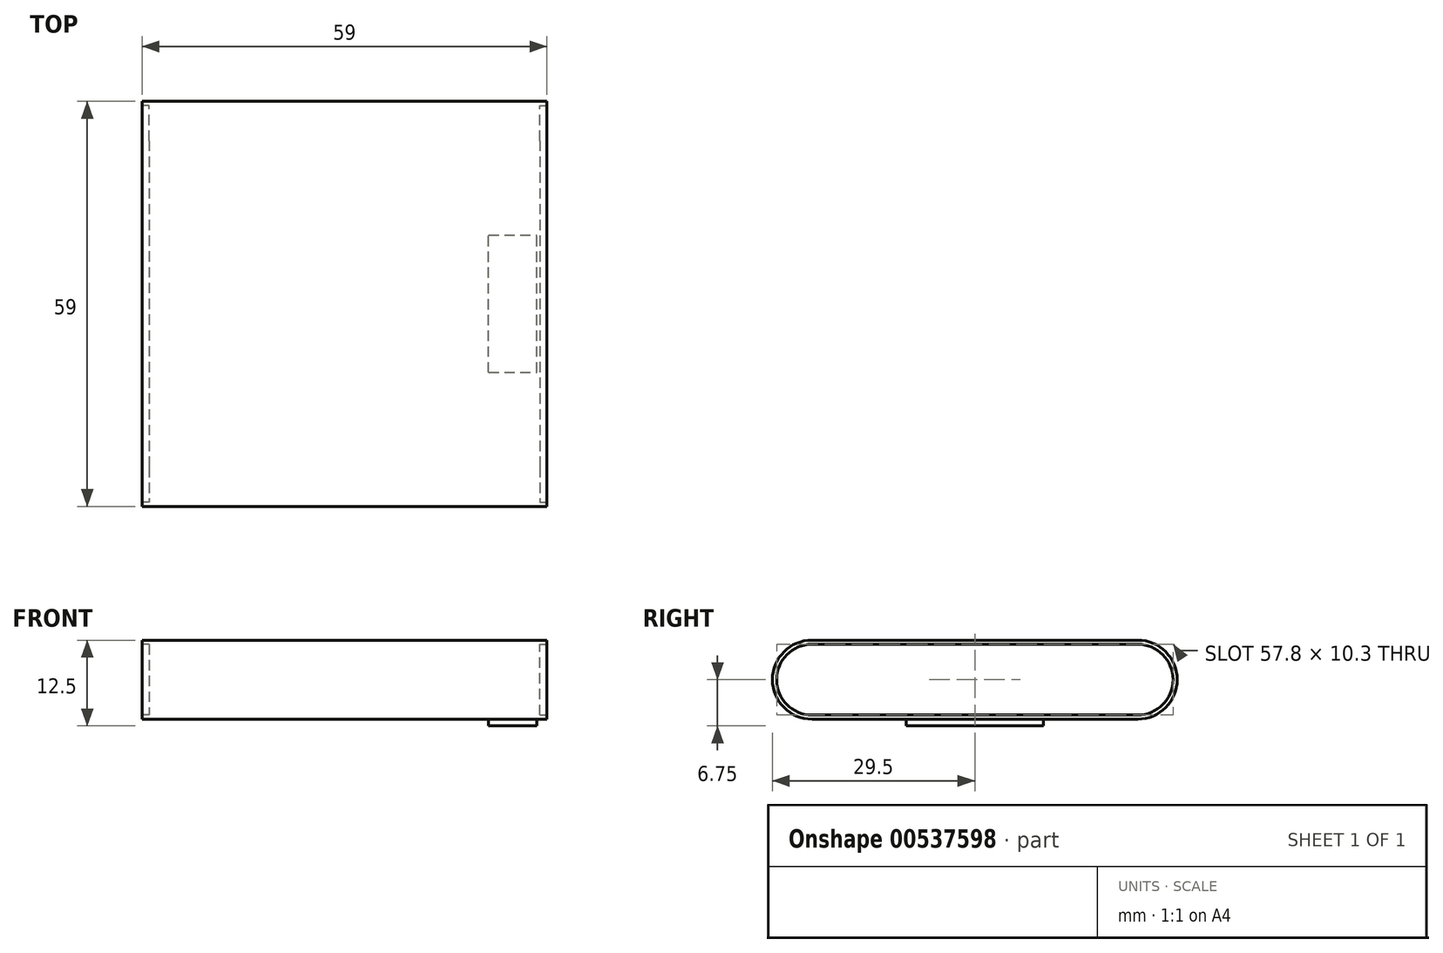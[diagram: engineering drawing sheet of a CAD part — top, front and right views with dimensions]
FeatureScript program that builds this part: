
annotation { "Feature Type Name" : "Feature", "Feature Type Description" : "" }
export const myFeature = defineFeature(function(context is Context, id is Id, definition is map)
    precondition{}
    {
        {
            var Q0;
            Q0=qCreatedBy(makeId("Top.planeOp"),FACE);
            var sketch = newSketch(context, id + "F0", { "sketchPlane" : qUnion([Q0])});
            skLineSegment(sketch, "E0.bottom", {"start": v(0, 0) * mm, "end": v(59, 0) * mm});
            skLineSegment(sketch, "E0.top", {"start": v(0, -59) * mm, "end": v(59, -59) * mm});
            skLineSegment(sketch, "E0.left", {"start": v(0, 0) * mm, "end": v(0, -59) * mm});
            skLineSegment(sketch, "E0.right", {"start": v(59, 0) * mm, "end": v(59, -59) * mm});
            skSolve(sketch);
        }
        {
            var Q0;
            Q0=qSketchRegion(id+"F0",true);
            extrude(context, id + "F1", {"entities" : qUnion([Q0]), "depth" : 11.5 * mm, "offsetDistance" : 25 * mm});
        }
        {
            var Q0;
            Q0=makeQuery(id+"F1.opExtrude","CAP_EDGE",EDGE,{"disambiguationData":[OSD([sQuery(id+"F0.wireOp",EDGE,"E0.top")])],"isStart":false});
            var Q1;
            Q1=makeQuery(id+"F1.opExtrude","CAP_EDGE",EDGE,{"disambiguationData":[OSD([sQuery(id+"F0.wireOp",EDGE,"E0.top")])],"isStart":true});
            var Q2;
            Q2=makeQuery(id+"F1.opExtrude","CAP_EDGE",EDGE,{"disambiguationData":[OSD([sQuery(id+"F0.wireOp",EDGE,"E0.bottom")])],"isStart":false});
            var Q3;
            Q3=makeQuery(id+"F1.opExtrude","CAP_EDGE",EDGE,{"disambiguationData":[OSD([sQuery(id+"F0.wireOp",EDGE,"E0.bottom")])],"isStart":true});
            fillet(context, id + "F2", {"entities" : qUnion([Q0, Q1, Q2, Q3]), "radius" : 5.75 * mm, "tangentPropagation" : true, "allowEdgeOverflow" : false});
        }
        {
            var Q0;
            Q0=makeQuery(id+"F1.opExtrude","SWEPT_FACE",FACE,{"disambiguationData":[OSD([sQuery(id+"F0.wireOp",EDGE,"E0.right")])]});
            var sketch = newSketch(context, id + "F3", { "sketchPlane" : qUnion([Q0])});
            skLineSegment(sketch, "E1.0", {"start": v(-5.75, 10.9) * mm, "end": v(-53.25, 10.9) * mm});
            skArc(sketch, "E1.1", {"start": v(-5.75, 0.6) * mm, "mid": v(-0.6, 5.75) * mm, "end": v(-5.75, 10.9) * mm});
            skLineSegment(sketch, "E1.2", {"start": v(-5.75, 0.6) * mm, "end": v(-53.25, 0.6) * mm});
            skArc(sketch, "E1.3", {"start": v(-53.25, 10.9) * mm, "mid": v(-58.4, 5.75) * mm, "end": v(-53.25, 0.6) * mm});
            skSolve(sketch);
        }
        {
            var Q0;
            Q0=qSketchRegion(id+"F3",true);
            extrude(context, id + "F4", {"entities" : qUnion([Q0]), "operationType" : NewBodyOperationType.REMOVE, "oppositeDirection" : true, "depth" : 1 * mm, "offsetDistance" : 25 * mm});
        }
        {
            var Q0;
            Q0=makeQuery(id+"F1.opExtrude","SWEPT_FACE",FACE,{"disambiguationData":[OSD([sQuery(id+"F0.wireOp",EDGE,"E0.left")])]});
            var sketch = newSketch(context, id + "F5", { "sketchPlane" : qUnion([Q0])});
            skLineSegment(sketch, "E2.0", {"start": v(5.75, 10.9) * mm, "end": v(53.25, 10.9) * mm});
            skArc(sketch, "E2.1", {"start": v(5.75, 10.9) * mm, "mid": v(0.6, 5.75) * mm, "end": v(5.75, 0.6) * mm});
            skLineSegment(sketch, "E2.2", {"start": v(5.75, 0.6) * mm, "end": v(53.25, 0.6) * mm});
            skArc(sketch, "E2.3", {"start": v(53.25, 0.6) * mm, "mid": v(58.4, 5.75) * mm, "end": v(53.25, 10.9) * mm});
            skSolve(sketch);
        }
        {
            var Q0;
            Q0=qSketchRegion(id+"F5",true);
            extrude(context, id + "F6", {"entities" : qUnion([Q0]), "operationType" : NewBodyOperationType.REMOVE, "oppositeDirection" : true, "depth" : 1 * mm, "offsetDistance" : 25 * mm});
        }
        {
            var Q0;
            Q0=makeQuery(id+"F1.opExtrude","CAP_FACE",FACE,{"disambiguationData":[OSD([sQuery(id+"F0.wireOp",EDGE,"E0.bottom"),sQuery(id+"F0.wireOp",EDGE,"E0.top"),sQuery(id+"F0.wireOp",EDGE,"E0.left"),sQuery(id+"F0.wireOp",EDGE,"E0.right")])],"isStart":true});
            var sketch = newSketch(context, id + "F7", { "sketchPlane" : qUnion([Q0])});
            skLineSegment(sketch, "E3", {"start": v(0, 0) * mm, "end": v(0, 5.75) * mm});
            skLineSegment(sketch, "E4", {"start": v(0, 5.75) * mm, "end": v(29.5, 5.75) * mm});
            skLineSegment(sketch, "E5", {"start": v(59, 29.5) * mm, "end": v(54, 29.5) * mm});
            skPoint(sketch, "E5.endSnap0", {"position": v(59, 29.5) * mm});
            skLineSegment(sketch, "E6.bottom", {"start": v(50.5, 39.5) * mm, "end": v(57.5, 39.5) * mm});
            skLineSegment(sketch, "E6.top", {"start": v(50.5, 19.5) * mm, "end": v(57.5, 19.5) * mm});
            skLineSegment(sketch, "E6.left", {"start": v(50.5, 39.5) * mm, "end": v(50.5, 19.5) * mm});
            skLineSegment(sketch, "E6.right", {"start": v(57.5, 39.5) * mm, "end": v(57.5, 19.5) * mm});
            skPoint(sketch, "E6.middle", {"position": v(54, 29.5) * mm});
            skSolve(sketch);
        }
        {
            var Q0;
            Q0 = qSketchRegion(id + "F7", true);
            extrude(context, id + "F8", {"entities" : qUnion([Q0]), "depth" : 1 * mm, "offsetDistance" : 25 * mm});
        }
    });
